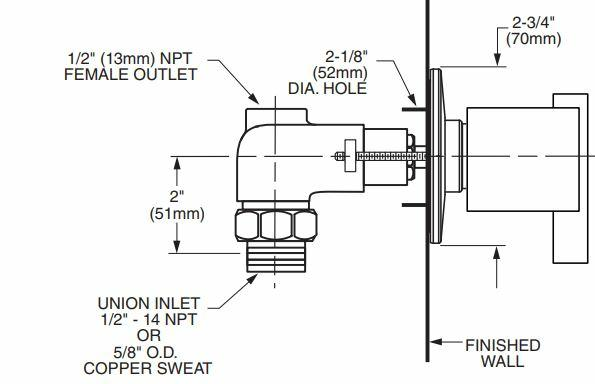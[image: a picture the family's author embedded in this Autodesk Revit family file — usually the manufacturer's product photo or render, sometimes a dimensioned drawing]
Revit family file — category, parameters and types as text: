
# Revit family: Diverter-American_Standard-Berwick-T430_Series
name_source: partatom
category: Plumbing Fixtures
revit_build: Autodesk Revit 2015 (Build: 20140606_1530(x64)
units: mm (PartAtom-declared; Revit-internal decimal feet)

## types (2) — shared parameters
Assembly Code = D2020300
CW Connection = Yes
Cold Water Connection Diameter = 1/2"
Cold Water Connection Radius = 1/4"
Default Elevation = 48"
Description = Berwick Diverter Valve Trim Kit
HW Connection = Yes
Height = 3"
Hot Water Connection Diameter = 1"
Hot Water Connection Radius = 1/4"
Installation Type = Wall Mounted
Length = 3 7/8"
Manufacturer = American Standard
Price = Prices may vary. Please consult Manufacturer Representative for most up-to-date price list.
Product Documentation Link = https://www.americanstandard-us.com
Product Page URL = https://www.americanstandard-us.com
Tempered Water Connection Diameter = 1/2"
Tempered Water Connection Radius = 1/4"
URL = https://www.americanstandard-us.com
Width = 2 3/4"

## per-type parameters (varying)
| type | Finish | Material |
| T430.430.002 | Metal-American Standard-002-Chrome | Metal-American Standard-002-Chrome |
| T430.430.295 | Brass-American Standard-295-Brushed Nickel | Brass-American Standard-295-Brushed Nickel |

note: column(s) folded — value = type name in every type: Model

## geometry (parser evidence)
native form markers: Sweep x3
no freeform markers — native parametric forms only
